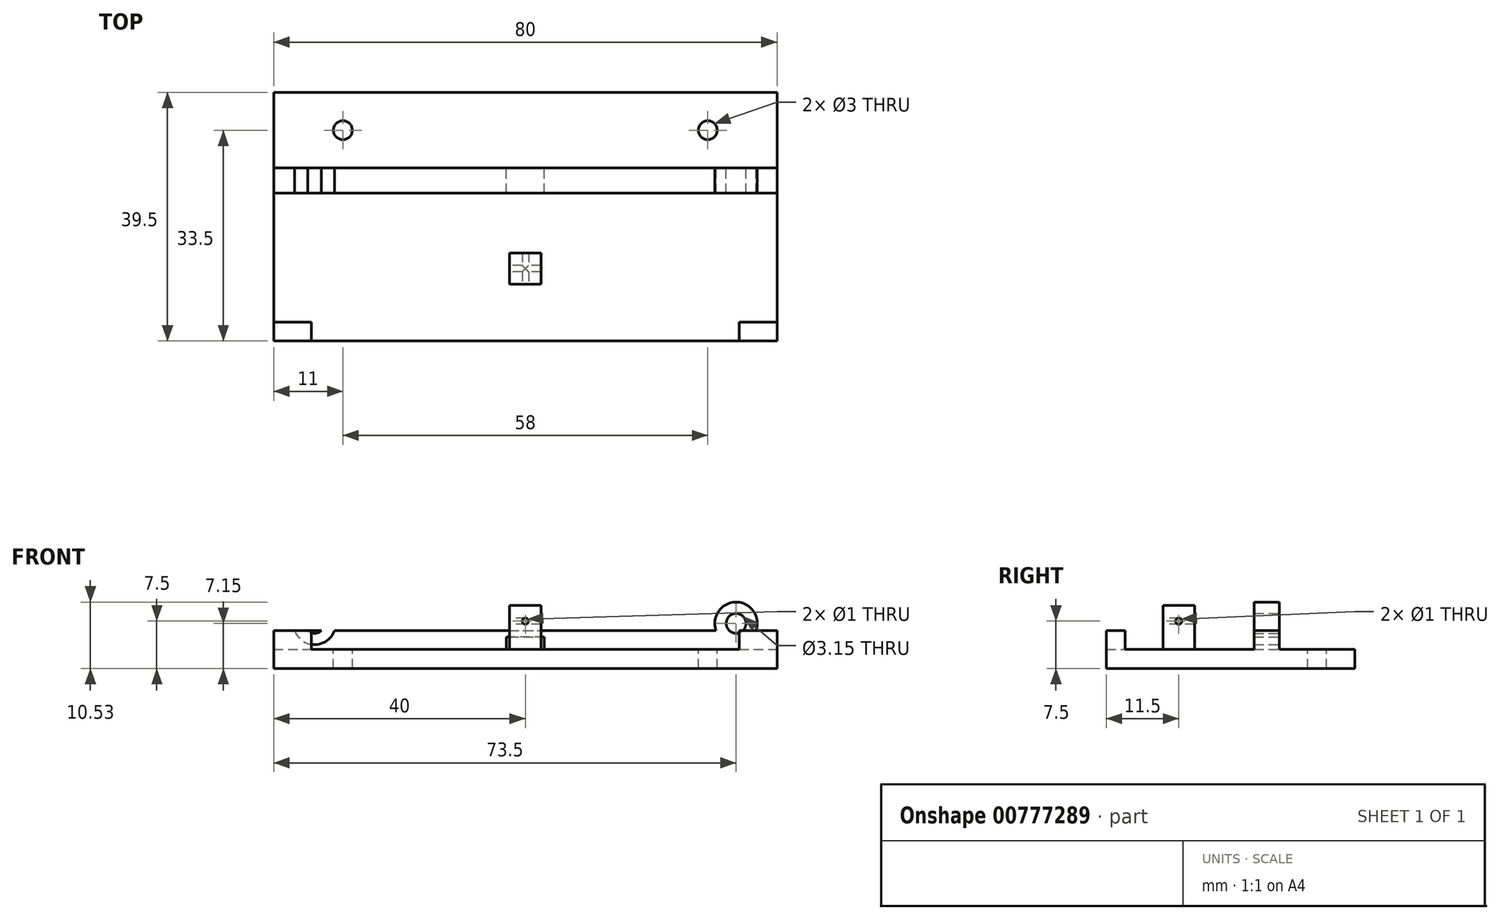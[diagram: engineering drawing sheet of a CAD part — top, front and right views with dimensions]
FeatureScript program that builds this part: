
annotation { "Feature Type Name" : "Feature", "Feature Type Description" : "" }
export const myFeature = defineFeature(function(context is Context, id is Id, definition is map)
    precondition{}
    {
        {
            var Q0;
            Q0=qCreatedBy(makeId("Top.planeOp"),FACE);
            var sketch = newSketch(context, id + "F0", { "sketchPlane" : qUnion([Q0])});
            skLineSegment(sketch, "E0.bottom", {"start": v(-40, 13.75) * mm, "end": v(40, 13.75) * mm});
            skLineSegment(sketch, "E0.top", {"start": v(-40, -13.75) * mm, "end": v(40, -13.75) * mm});
            skLineSegment(sketch, "E0.left", {"start": v(-40, 13.75) * mm, "end": v(-40, -13.75) * mm});
            skLineSegment(sketch, "E0.right", {"start": v(40, 13.75) * mm, "end": v(40, -13.75) * mm});
            skLineSegment(sketch, "E1", {"start": v(-20.15, 0) * mm, "end": v(9.85, 0) * mm, "construction": true});
            skLineSegment(sketch, "E2", {"start": v(0, 36.74) * mm, "end": v(0, -42.86) * mm, "construction": true});
            skSolve(sketch);
        }
        {
            var Q0;
            Q0=makeQuery(id+"F0.imprint","IMPRINT",FACE,{"disambiguationData":[TD([[makeQuery(id+"F0.imprint","IMPRINT",EDGE,{"derivedFrom":sQuery(id+"F0.wireOp",EDGE,"E0.bottom")}),-1.0]])]});
            extrude(context, id + "F1", {"entities" : qUnion([Q0]), "depth" : 3 * mm, "offsetDistance" : 25 * mm});
        }
        {
            var Q0;
            Q0=makeQuery(id+"F1.opExtrude","CAP_FACE",FACE,{"disambiguationData":[OSD([sQuery(id+"F0.wireOp",EDGE,"E0.bottom"),sQuery(id+"F0.wireOp",EDGE,"E0.top"),sQuery(id+"F0.wireOp",EDGE,"E0.left"),sQuery(id+"F0.wireOp",EDGE,"E0.right")])],"isStart":false});
            var sketch = newSketch(context, id + "F2", { "sketchPlane" : qUnion([Q0])});
            skLineSegment(sketch, "E3.bottom", {"start": v(-40, -13.75) * mm, "end": v(-34, -13.75) * mm});
            skLineSegment(sketch, "E3.top", {"start": v(-40, -10.75) * mm, "end": v(-34, -10.75) * mm});
            skLineSegment(sketch, "E3.left", {"start": v(-40, -13.75) * mm, "end": v(-40, -10.75) * mm});
            skLineSegment(sketch, "E3.right", {"start": v(-34, -13.75) * mm, "end": v(-34, -10.75) * mm});
            skLineSegment(sketch, "E4.bottom", {"start": v(40, -13.75) * mm, "end": v(34, -13.75) * mm});
            skLineSegment(sketch, "E4.top", {"start": v(40, -10.75) * mm, "end": v(34, -10.75) * mm});
            skLineSegment(sketch, "E4.left", {"start": v(40, -13.75) * mm, "end": v(40, -10.75) * mm});
            skLineSegment(sketch, "E4.right", {"start": v(34, -13.75) * mm, "end": v(34, -10.75) * mm});
            skLineSegment(sketch, "E5.bottom", {"start": v(-2.5, 0.25) * mm, "end": v(2.5, 0.25) * mm});
            skLineSegment(sketch, "E5.top", {"start": v(-2.5, -4.75) * mm, "end": v(2.5, -4.75) * mm});
            skLineSegment(sketch, "E5.left", {"start": v(-2.5, 0.25) * mm, "end": v(-2.5, -4.75) * mm});
            skLineSegment(sketch, "E5.right", {"start": v(2.5, 0.25) * mm, "end": v(2.5, -4.75) * mm});
            skLineSegment(sketch, "E6", {"start": v(-40, 9.75) * mm, "end": v(40, 9.75) * mm});
            skSolve(sketch);
        }
        {
            var Q0;
            {var subQ0=sQuery(id+"F2.wireOp",EDGE,"E6");Q0=makeQuery(id+"F2.imprint","IMPRINT",FACE,{"disambiguationData":[TD([[makeQuery(id+"F2.imprint","IMPRINT",EDGE,{"derivedFrom":subQ0}),1.0]])]});}
            var Q1;
            Q1=makeQuery(id+"F2.imprint","IMPRINT",FACE,{"disambiguationData":[TD([[makeQuery(id+"F2.imprint","IMPRINT",EDGE,{"derivedFrom":sQuery(id+"F2.wireOp",EDGE,"E3.bottom")}),1.0]])]});
            var Q2;
            Q2=makeQuery(id+"F2.imprint","IMPRINT",FACE,{"disambiguationData":[TD([[makeQuery(id+"F2.imprint","IMPRINT",EDGE,{"derivedFrom":sQuery(id+"F2.wireOp",EDGE,"E4.bottom")}),1.0]])]});
            extrude(context, id + "F3", {"entities" : qUnion([Q0, Q1, Q2]), "operationType" : NewBodyOperationType.ADD, "depth" : 3 * mm, "offsetDistance" : 25 * mm});
        }
        {
            var Q0;
            Q0=makeQuery(id+"F2.imprint","IMPRINT",FACE,{"disambiguationData":[TD([[makeQuery(id+"F2.imprint","IMPRINT",EDGE,{"derivedFrom":sQuery(id+"F2.wireOp",EDGE,"E5.bottom")}),-1.0]])]});
            extrude(context, id + "F4", {"entities" : qUnion([Q0]), "operationType" : NewBodyOperationType.ADD, "depth" : 7 * mm, "offsetDistance" : 25 * mm});
        }
        {
            var Q0;
            Q0=makeQuery(id+"F4.opExtrude","SWEPT_FACE",FACE,{"disambiguationData":[OSD([sQuery(id+"F2.wireOp",EDGE,"E5.top")])]});
            var sketch = newSketch(context, id + "F5", { "sketchPlane" : qUnion([Q0])});
            skLineSegment(sketch, "E7", {"start": v(-2.5, 7.5) * mm, "end": v(2.5, 7.5) * mm, "construction": true});
            skCircle(sketch, "E8", {"center": v(0, 7.5) * mm, "radius": 0.5 * mm});
            skSolve(sketch);
        }
        {
            var Q0;
            Q0=makeQuery(id+"F5.imprint","IMPRINT",FACE,{"disambiguationData":[TD([[makeQuery(id+"F5.imprint","IMPRINT",EDGE,{"derivedFrom":sQuery(id+"F5.wireOp",EDGE,"E8")}),1.0]])]});
            extrude(context, id + "F6", {"entities" : qUnion([Q0]), "operationType" : NewBodyOperationType.REMOVE, "oppositeDirection" : true, "depth" : 5 * mm, "offsetDistance" : 25 * mm});
        }
        {
            var Q0;
            {var subQ0=sQuery(id+"F0.wireOp",EDGE,"E0.bottom");Q0=makeQuery(id+"F3.boolean.opBoolean","MERGE",FACE,{"derivedFrom":[makeQuery(id+"F1.opExtrude","SWEPT_FACE",FACE,{"disambiguationData":[OSD([subQ0])]}),makeQuery(id+"F3.opExtrude","SWEPT_FACE",FACE,{"disambiguationData":[OSD([subQ0])]})]});}
            var sketch = newSketch(context, id + "F7", { "sketchPlane" : qUnion([Q0])});
            skLineSegment(sketch, "E9.bottom", {"start": v(-3, 5) * mm, "end": v(3, 5) * mm});
            skLineSegment(sketch, "E9.top", {"start": v(-3, 3) * mm, "end": v(3, 3) * mm});
            skLineSegment(sketch, "E9.left", {"start": v(-3, 5) * mm, "end": v(-3, 3) * mm});
            skLineSegment(sketch, "E9.right", {"start": v(3, 5) * mm, "end": v(3, 3) * mm});
            skLineSegment(sketch, "E10", {"start": v(0, 0) * mm, "end": v(0, 6) * mm, "construction": true});
            skSolve(sketch);
        }
        {
            var Q0;
            Q0=makeQuery(id+"F7.imprint","IMPRINT",FACE,{"disambiguationData":[TD([[makeQuery(id+"F7.imprint","IMPRINT",EDGE,{"derivedFrom":sQuery(id+"F7.wireOp",EDGE,"E9.bottom")}),-1.0]])]});
            extrude(context, id + "F8", {"entities" : qUnion([Q0]), "operationType" : NewBodyOperationType.REMOVE, "endBound" : BoundingType.UP_TO_NEXT, "oppositeDirection" : true, "depth" : 25 * mm, "offsetDistance" : 25 * mm});
        }
        {
            var Q0;
            {var subQ0=sQuery(id+"F0.wireOp",EDGE,"E0.bottom");Q0=makeQuery(id+"F3.boolean.opBoolean","MERGE",FACE,{"derivedFrom":[makeQuery(id+"F1.opExtrude","SWEPT_FACE",FACE,{"disambiguationData":[OSD([subQ0])]}),makeQuery(id+"F3.opExtrude","SWEPT_FACE",FACE,{"disambiguationData":[OSD([subQ0])]})]});}
            var sketch = newSketch(context, id + "F9", { "sketchPlane" : qUnion([Q0])});
            skCircle(sketch, "E11", {"center": v(-33.5, 7.15) * mm, "radius": 3.38 * mm});
            skCircle(sketch, "E12", {"center": v(-33.5, 7.15) * mm, "radius": 1.57 * mm});
            skLineSegment(sketch, "E13", {"start": v(0, 0) * mm, "end": v(0, 6) * mm, "construction": true});
            skCircle(sketch, "E14.MirrorC", {"center": v(33.5, 7.15) * mm, "radius": 3.38 * mm});
            skCircle(sketch, "E15.MirrorC", {"center": v(33.5, 7.15) * mm, "radius": 1.57 * mm});
            skSolve(sketch);
        }
        {
            var Q0;
            {var subQ0=sQuery(id+"F9.wireOp",EDGE,"E11");var subQ1=makeQuery(id+"F3.opExtrude","CAP_EDGE",EDGE,{"disambiguationData":[OSD([sQuery(id+"F0.wireOp",EDGE,"E0.bottom")])],"isStart":false});var subQ2=makeQuery(id+"F9.imprint","INTERSECT",VERTEX,{"disambiguationData":[OD(0.0)],"derivedFrom":[subQ1,subQ0]});Q0=makeQuery(id+"F9.imprint","IMPRINT",FACE,{"disambiguationData":[TD([[makeQuery(id+"F9.imprint","IMPRINT",EDGE,{"disambiguationData":[TD([[subQ2,-1.0]])],"derivedFrom":subQ0}),1.0]])]});}
            var Q1;
            {var subQ0=sQuery(id+"F9.wireOp",EDGE,"E11");var subQ1=makeQuery(id+"F3.opExtrude","CAP_EDGE",EDGE,{"disambiguationData":[OSD([sQuery(id+"F0.wireOp",EDGE,"E0.bottom")])],"isStart":false});var subQ2=makeQuery(id+"F9.imprint","INTERSECT",VERTEX,{"disambiguationData":[OD(0.0)],"derivedFrom":[subQ1,subQ0]});Q1=makeQuery(id+"F9.imprint","IMPRINT",FACE,{"disambiguationData":[TD([[makeQuery(id+"F9.imprint","IMPRINT",EDGE,{"disambiguationData":[TD([[subQ2,1.0]])],"derivedFrom":subQ0}),1.0]])]});}
            var Q2;
            {var subQ0=sQuery(id+"F9.wireOp",EDGE,"E12");var subQ1=makeQuery(id+"F3.opExtrude","CAP_EDGE",EDGE,{"disambiguationData":[OSD([sQuery(id+"F0.wireOp",EDGE,"E0.bottom")])],"isStart":false});var subQ2=makeQuery(id+"F9.imprint","INTERSECT",VERTEX,{"disambiguationData":[OD(0.0)],"derivedFrom":[subQ1,subQ0]});Q2=makeQuery(id+"F9.imprint","IMPRINT",FACE,{"disambiguationData":[TD([[makeQuery(id+"F9.imprint","IMPRINT",EDGE,{"disambiguationData":[TD([[subQ2,1.0]])],"derivedFrom":subQ0}),1.0]])]});}
            var Q3;
            {var subQ0=sQuery(id+"F9.wireOp",EDGE,"E12");var subQ1=makeQuery(id+"F3.opExtrude","CAP_EDGE",EDGE,{"disambiguationData":[OSD([sQuery(id+"F0.wireOp",EDGE,"E0.bottom")])],"isStart":false});var subQ2=makeQuery(id+"F9.imprint","INTERSECT",VERTEX,{"disambiguationData":[OD(0.0)],"derivedFrom":[subQ1,subQ0]});Q3=makeQuery(id+"F9.imprint","IMPRINT",FACE,{"disambiguationData":[TD([[makeQuery(id+"F9.imprint","IMPRINT",EDGE,{"disambiguationData":[TD([[subQ2,-1.0]])],"derivedFrom":subQ0}),1.0]])]});}
            extrude(context, id + "F10", {"entities" : qUnion([Q0, Q1, Q2, Q3]), "operationType" : NewBodyOperationType.ADD, "oppositeDirection" : true, "depth" : 4 * mm, "offsetDistance" : 25 * mm});
        }
        {
            var Q0;
            {var subQ0=sQuery(id+"F9.wireOp",EDGE,"E12");var subQ1=makeQuery(id+"F3.opExtrude","CAP_EDGE",EDGE,{"disambiguationData":[OSD([sQuery(id+"F0.wireOp",EDGE,"E0.bottom")])],"isStart":false});var subQ2=makeQuery(id+"F9.imprint","INTERSECT",VERTEX,{"disambiguationData":[OD(0.0)],"derivedFrom":[subQ1,subQ0]});Q0=makeQuery(id+"F9.imprint","IMPRINT",FACE,{"disambiguationData":[TD([[makeQuery(id+"F9.imprint","IMPRINT",EDGE,{"disambiguationData":[TD([[subQ2,1.0]])],"derivedFrom":subQ0}),1.0]])]});}
            var Q1;
            {var subQ0=sQuery(id+"F9.wireOp",EDGE,"E12");var subQ1=makeQuery(id+"F3.opExtrude","CAP_EDGE",EDGE,{"disambiguationData":[OSD([sQuery(id+"F0.wireOp",EDGE,"E0.bottom")])],"isStart":false});var subQ2=makeQuery(id+"F9.imprint","INTERSECT",VERTEX,{"disambiguationData":[OD(0.0)],"derivedFrom":[subQ1,subQ0]});Q1=makeQuery(id+"F9.imprint","IMPRINT",FACE,{"disambiguationData":[TD([[makeQuery(id+"F9.imprint","IMPRINT",EDGE,{"disambiguationData":[TD([[subQ2,-1.0]])],"derivedFrom":subQ0}),1.0]])]});}
            extrude(context, id + "F11", {"entities" : qUnion([Q0, Q1]), "operationType" : NewBodyOperationType.REMOVE, "endBound" : BoundingType.UP_TO_NEXT, "oppositeDirection" : true, "depth" : 25 * mm, "offsetDistance" : 25 * mm});
        }
        {
            var Q0;
            {var subQ0=sQuery(id+"F9.wireOp",EDGE,"E14.MirrorC");var subQ1=makeQuery(id+"F3.opExtrude","CAP_EDGE",EDGE,{"disambiguationData":[OSD([sQuery(id+"F0.wireOp",EDGE,"E0.bottom")])],"isStart":false});var subQ2=makeQuery(id+"F9.imprint","INTERSECT",VERTEX,{"disambiguationData":[OD(0.0)],"derivedFrom":[subQ1,subQ0]});Q0=makeQuery(id+"F9.imprint","IMPRINT",FACE,{"disambiguationData":[TD([[makeQuery(id+"F9.imprint","IMPRINT",EDGE,{"disambiguationData":[TD([[subQ2,1.0]])],"derivedFrom":subQ0}),-1.0]])]});}
            var Q1;
            {var subQ0=sQuery(id+"F9.wireOp",EDGE,"E15.MirrorC");var subQ1=makeQuery(id+"F3.opExtrude","CAP_EDGE",EDGE,{"disambiguationData":[OSD([sQuery(id+"F0.wireOp",EDGE,"E0.bottom")])],"isStart":false});var subQ2=makeQuery(id+"F9.imprint","INTERSECT",VERTEX,{"disambiguationData":[OD(0.0)],"derivedFrom":[subQ1,subQ0]});Q1=makeQuery(id+"F9.imprint","IMPRINT",FACE,{"disambiguationData":[TD([[makeQuery(id+"F9.imprint","IMPRINT",EDGE,{"disambiguationData":[TD([[subQ2,1.0]])],"derivedFrom":subQ0}),-1.0]])]});}
            var Q2;
            {var subQ0=sQuery(id+"F9.wireOp",EDGE,"E15.MirrorC");var subQ1=makeQuery(id+"F3.opExtrude","CAP_EDGE",EDGE,{"disambiguationData":[OSD([sQuery(id+"F0.wireOp",EDGE,"E0.bottom")])],"isStart":false});var subQ2=makeQuery(id+"F9.imprint","INTERSECT",VERTEX,{"disambiguationData":[OD(0.0)],"derivedFrom":[subQ1,subQ0]});Q2=makeQuery(id+"F9.imprint","IMPRINT",FACE,{"disambiguationData":[TD([[makeQuery(id+"F9.imprint","IMPRINT",EDGE,{"disambiguationData":[TD([[subQ2,-1.0]])],"derivedFrom":subQ0}),-1.0]])]});}
            var Q3;
            {var subQ0=sQuery(id+"F9.wireOp",EDGE,"E14.MirrorC");var subQ1=makeQuery(id+"F3.opExtrude","CAP_EDGE",EDGE,{"disambiguationData":[OSD([sQuery(id+"F0.wireOp",EDGE,"E0.bottom")])],"isStart":false});var subQ2=makeQuery(id+"F9.imprint","INTERSECT",VERTEX,{"disambiguationData":[OD(0.0)],"derivedFrom":[subQ1,subQ0]});Q3=makeQuery(id+"F9.imprint","IMPRINT",FACE,{"disambiguationData":[TD([[makeQuery(id+"F9.imprint","IMPRINT",EDGE,{"disambiguationData":[TD([[subQ2,-1.0]])],"derivedFrom":subQ0}),-1.0]])]});}
            extrude(context, id + "F12", {"entities" : qUnion([Q0, Q1, Q2, Q3]), "operationType" : NewBodyOperationType.ADD, "oppositeDirection" : true, "depth" : 4 * mm, "offsetDistance" : 25 * mm});
        }
        {
            var Q0;
            {var subQ0=sQuery(id+"F9.wireOp",EDGE,"E15.MirrorC");var subQ1=makeQuery(id+"F3.opExtrude","CAP_EDGE",EDGE,{"disambiguationData":[OSD([sQuery(id+"F0.wireOp",EDGE,"E0.bottom")])],"isStart":false});var subQ2=makeQuery(id+"F9.imprint","INTERSECT",VERTEX,{"disambiguationData":[OD(0.0)],"derivedFrom":[subQ1,subQ0]});Q0=makeQuery(id+"F9.imprint","IMPRINT",FACE,{"disambiguationData":[TD([[makeQuery(id+"F9.imprint","IMPRINT",EDGE,{"disambiguationData":[TD([[subQ2,1.0]])],"derivedFrom":subQ0}),-1.0]])]});}
            var Q1;
            {var subQ0=sQuery(id+"F9.wireOp",EDGE,"E15.MirrorC");var subQ1=makeQuery(id+"F3.opExtrude","CAP_EDGE",EDGE,{"disambiguationData":[OSD([sQuery(id+"F0.wireOp",EDGE,"E0.bottom")])],"isStart":false});var subQ2=makeQuery(id+"F9.imprint","INTERSECT",VERTEX,{"disambiguationData":[OD(0.0)],"derivedFrom":[subQ1,subQ0]});Q1=makeQuery(id+"F9.imprint","IMPRINT",FACE,{"disambiguationData":[TD([[makeQuery(id+"F9.imprint","IMPRINT",EDGE,{"disambiguationData":[TD([[subQ2,-1.0]])],"derivedFrom":subQ0}),-1.0]])]});}
            extrude(context, id + "F13", {"entities" : qUnion([Q0, Q1]), "operationType" : NewBodyOperationType.REMOVE, "endBound" : BoundingType.UP_TO_NEXT, "oppositeDirection" : true, "depth" : 25 * mm, "offsetDistance" : 25 * mm});
        }
        {
            var Q0;
            {var subQ1=sQuery(id+"F0.wireOp",EDGE,"E0.bottom");Q0=makeQuery(id+"F9.imprint","IMPRINT",FACE,{"disambiguationData":[TD([[makeQuery(id+"F9.imprint","IMPRINT",EDGE,{"derivedFrom":makeQuery(id+"F1.opExtrude","CAP_EDGE",EDGE,{"disambiguationData":[OSD([subQ1])],"isStart":true})}),-1.0]])]});}
            var sketch = newSketch(context, id + "F14", { "sketchPlane" : qUnion([Q0])});
            skLineSegment(sketch, "E16.bottom", {"start": v(-40, 0) * mm, "end": v(40, 0) * mm});
            skLineSegment(sketch, "E16.top", {"start": v(-40, 3) * mm, "end": v(40, 3) * mm});
            skLineSegment(sketch, "E16.left", {"start": v(-40, 0) * mm, "end": v(-40, 3) * mm});
            skLineSegment(sketch, "E16.right", {"start": v(40, 0) * mm, "end": v(40, 3) * mm});
            skSolve(sketch);
        }
        {
            var Q0;
            Q0=makeQuery(id+"F14.imprint","IMPRINT",FACE,{"disambiguationData":[TD([[makeQuery(id+"F14.imprint","IMPRINT",EDGE,{"derivedFrom":sQuery(id+"F14.wireOp",EDGE,"E16.bottom")}),-1.0]])]});
            extrude(context, id + "F15", {"entities" : qUnion([Q0]), "operationType" : NewBodyOperationType.ADD, "depth" : 12 * mm, "offsetDistance" : 25 * mm});
        }
        {
            var Q0;
            Q0=makeQuery(id+"F15.boolean.opBoolean","MERGE",FACE,{"derivedFrom":[makeQuery(id+"F8.boolean.opBoolean","MERGE",FACE,{"derivedFrom":[makeQuery(id+"F1.opExtrude","CAP_FACE",FACE,{"disambiguationData":[OSD([sQuery(id+"F0.wireOp",EDGE,"E0.bottom"),sQuery(id+"F0.wireOp",EDGE,"E0.top"),sQuery(id+"F0.wireOp",EDGE,"E0.left"),sQuery(id+"F0.wireOp",EDGE,"E0.right")])],"isStart":false}),makeQuery(id+"F8.opExtrude","SWEPT_FACE",FACE,{"disambiguationData":[OSD([sQuery(id+"F7.wireOp",EDGE,"E9.top")])]})]}),makeQuery(id+"F15.opExtrude","SWEPT_FACE",FACE,{"disambiguationData":[OSD([sQuery(id+"F14.wireOp",EDGE,"E16.top")])]})]});
            var sketch = newSketch(context, id + "F16", { "sketchPlane" : qUnion([Q0])});
            skCircle(sketch, "E17", {"center": v(29, 19.75) * mm, "radius": 1.5 * mm});
            skCircle(sketch, "E18", {"center": v(-29, 19.75) * mm, "radius": 1.5 * mm});
            skSolve(sketch);
        }
        {
            var Q0;
            Q0=makeQuery(id+"F16.imprint","IMPRINT",FACE,{"disambiguationData":[TD([[makeQuery(id+"F16.imprint","IMPRINT",EDGE,{"derivedFrom":sQuery(id+"F16.wireOp",EDGE,"E17")}),1.0]])]});
            var Q1;
            Q1=makeQuery(id+"F16.imprint","IMPRINT",FACE,{"disambiguationData":[TD([[makeQuery(id+"F16.imprint","IMPRINT",EDGE,{"derivedFrom":sQuery(id+"F16.wireOp",EDGE,"E18")}),1.0]])]});
            extrude(context, id + "F17", {"entities" : qUnion([Q0, Q1]), "operationType" : NewBodyOperationType.REMOVE, "endBound" : BoundingType.UP_TO_NEXT, "oppositeDirection" : true, "depth" : 25 * mm, "offsetDistance" : 25 * mm});
        }
        {
            var Q0;
            Q0=makeQuery(id+"F4.opExtrude","SWEPT_FACE",FACE,{"disambiguationData":[OSD([sQuery(id+"F2.wireOp",EDGE,"E5.left")])]});
            var sketch = newSketch(context, id + "F18", { "sketchPlane" : qUnion([Q0])});
            skLineSegment(sketch, "E19", {"start": v(2.25, 10) * mm, "end": v(2.25, 3) * mm, "construction": true});
            skCircle(sketch, "E20", {"center": v(2.25, 7.5) * mm, "radius": 0.5 * mm});
            skSolve(sketch);
        }
        {
            var Q0;
            Q0=makeQuery(id+"F18.imprint","IMPRINT",FACE,{"disambiguationData":[TD([[makeQuery(id+"F18.imprint","IMPRINT",EDGE,{"derivedFrom":sQuery(id+"F18.wireOp",EDGE,"E20")}),1.0]])]});
            extrude(context, id + "F19", {"entities" : qUnion([Q0]), "operationType" : NewBodyOperationType.REMOVE, "endBound" : BoundingType.THROUGH_ALL, "oppositeDirection" : true, "depth" : 25 * mm, "offsetDistance" : 25 * mm});
        }
    });
